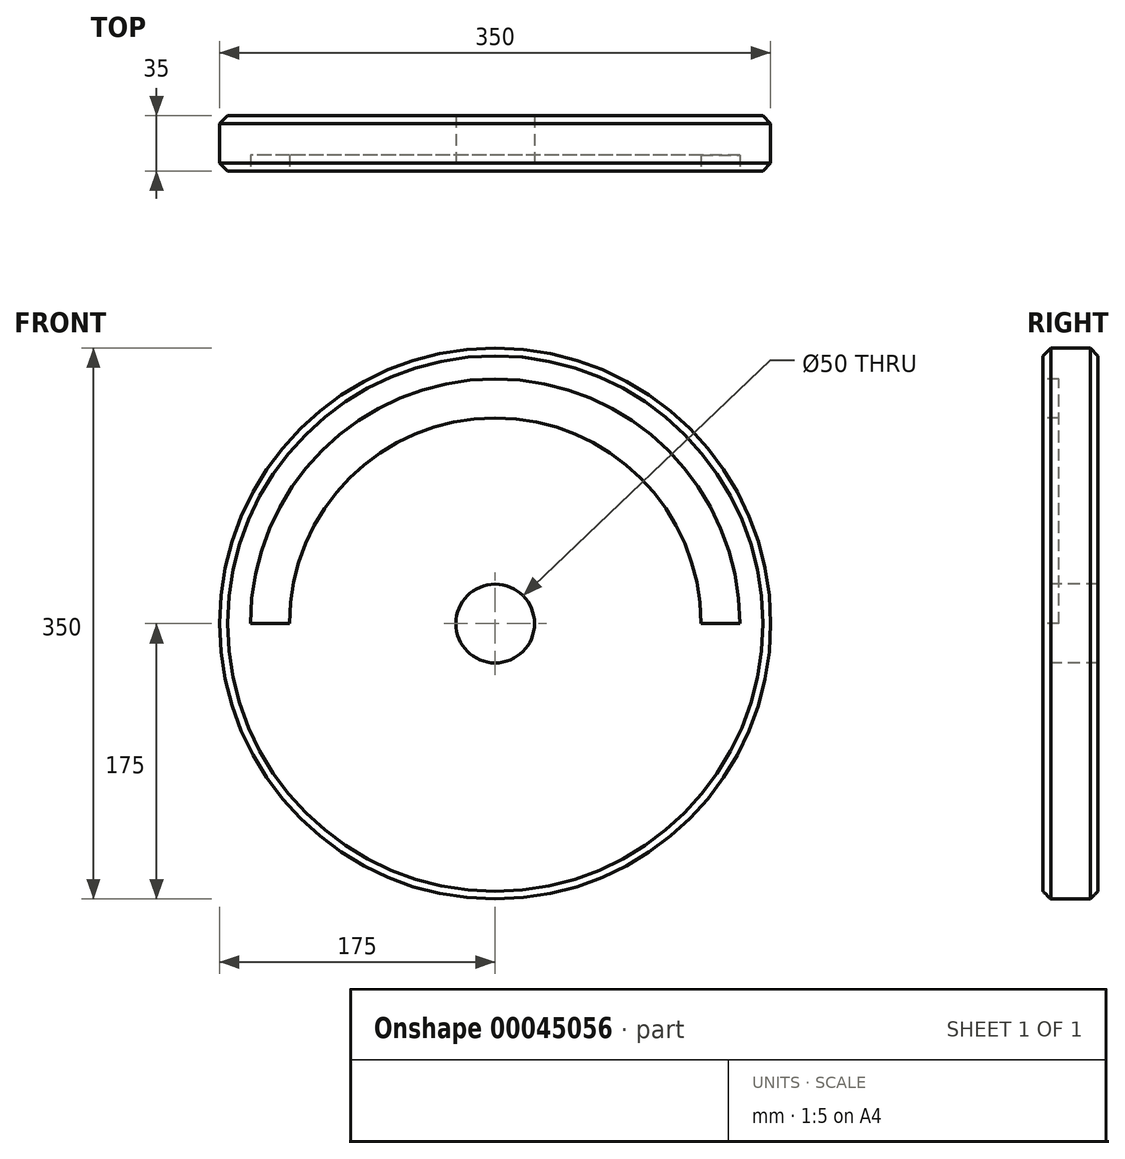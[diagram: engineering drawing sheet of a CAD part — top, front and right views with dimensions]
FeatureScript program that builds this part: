
annotation { "Feature Type Name" : "Feature", "Feature Type Description" : "" }
export const myFeature = defineFeature(function(context is Context, id is Id, definition is map)
    precondition{}
    {
        {
            var Q0;
            Q0=qCreatedBy(makeId("Front.planeOp"),FACE);
            var sketch = newSketch(context, id + "F0", { "sketchPlane" : qUnion([Q0])});
            skCircle(sketch, "E0", {"center": v(0, 0) * mm, "radius": 175 * mm});
            skSolve(sketch);
        }
        {
            var Q0;
            Q0=makeQuery(id+"F0.imprint","IMPRINT",FACE,{"disambiguationData":[TD([[makeQuery(id+"F0.imprint","IMPRINT",EDGE,{"derivedFrom":sQuery(id+"F0.wireOp",EDGE,"E0")}),1.0]])]});
            extrude(context, id + "F1", {"entities" : qUnion([Q0]), "depth" : 35 * mm});
        }
        {
            var Q0;
            Q0=makeQuery(id+"F1.opExtrude","CAP_FACE",FACE,{"disambiguationData":[OSD([sQuery(id+"F0.wireOp",EDGE,"E0")])],"isStart":false});
            var sketch = newSketch(context, id + "F2", { "sketchPlane" : qUnion([Q0])});
            skPoint(sketch, "E1", {"position": v(0, 0) * mm});
            skSolve(sketch);
        }
        {
            var Q0;
            Q0=sQuery(id+"F2.wireOp",VERTEX,"E1");
            var Q1;
            Q1=makeQuery(id+"F1.opExtrude","SWEPT_BODY",BODY,{"disambiguationData":[OSD([sQuery(id+"F0.wireOp",EDGE,"E0")])]});
            hole(context, id + "F3", {"style" : HoleStyle.SIMPLE, "holeDiameter" : 50 * mm, "endStyle" : HoleEndStyle.THROUGH, "locations" : qUnion([Q0]), "scope" : qUnion([Q1])});
        }
        {
            var Q0;
            Q0=makeQuery(id+"F1.opExtrude","CAP_EDGE",EDGE,{"disambiguationData":[OSD([sQuery(id+"F0.wireOp",EDGE,"E0")])],"isStart":false});
            var Q1;
            Q1=makeQuery(id+"F1.opExtrude","CAP_EDGE",EDGE,{"disambiguationData":[OSD([sQuery(id+"F0.wireOp",EDGE,"E0")])],"isStart":true});
            chamfer(context, id + "F4", {"entities" : qUnion([Q0, Q1]), "width" : 5 * mm, "tangentPropagation" : true});
        }
        {
            var Q0;
            Q0=makeQuery(id+"F1.opExtrude","CAP_FACE",FACE,{"disambiguationData":[OSD([sQuery(id+"F0.wireOp",EDGE,"E0")])],"isStart":false});
            var sketch = newSketch(context, id + "F5", { "sketchPlane" : qUnion([Q0])});
            skLineSegment(sketch, "E2", {"start": v(0, 0) * mm, "end": v(-155.46, 0) * mm});
            skLineSegment(sketch, "E3", {"start": v(0, 0) * mm, "end": v(155.46, 0) * mm});
            skArc(sketch, "E4", {"start": v(-130.68, 0) * mm, "mid": v(0, -130.68) * mm, "end": v(130.68, 0) * mm});
            skArc(sketch, "E5", {"start": v(130.68, 0) * mm, "mid": v(0, 130.68) * mm, "end": v(-130.68, 0) * mm});
            skArc(sketch, "E6", {"start": v(-155.46, 0) * mm, "mid": v(0, -155.46) * mm, "end": v(155.46, 0) * mm});
            skArc(sketch, "E7", {"start": v(155.46, 0) * mm, "mid": v(0, 155.46) * mm, "end": v(-155.46, 0) * mm});
            skSolve(sketch);
        }
        {
            var Q0;
            {var subQ1=sQuery(id+"F5.wireOp",EDGE,"E5");Q0=makeQuery(id+"F5.imprint","IMPRINT",FACE,{"disambiguationData":[TD([[makeQuery(id+"F5.imprint","IMPRINT",EDGE,{"derivedFrom":subQ1}),-1.0]])]});}
            extrude(context, id + "F6", {"entities" : qUnion([Q0]), "operationType" : NewBodyOperationType.REMOVE, "oppositeDirection" : true, "depth" : 10.22 * mm});
        }
    });
